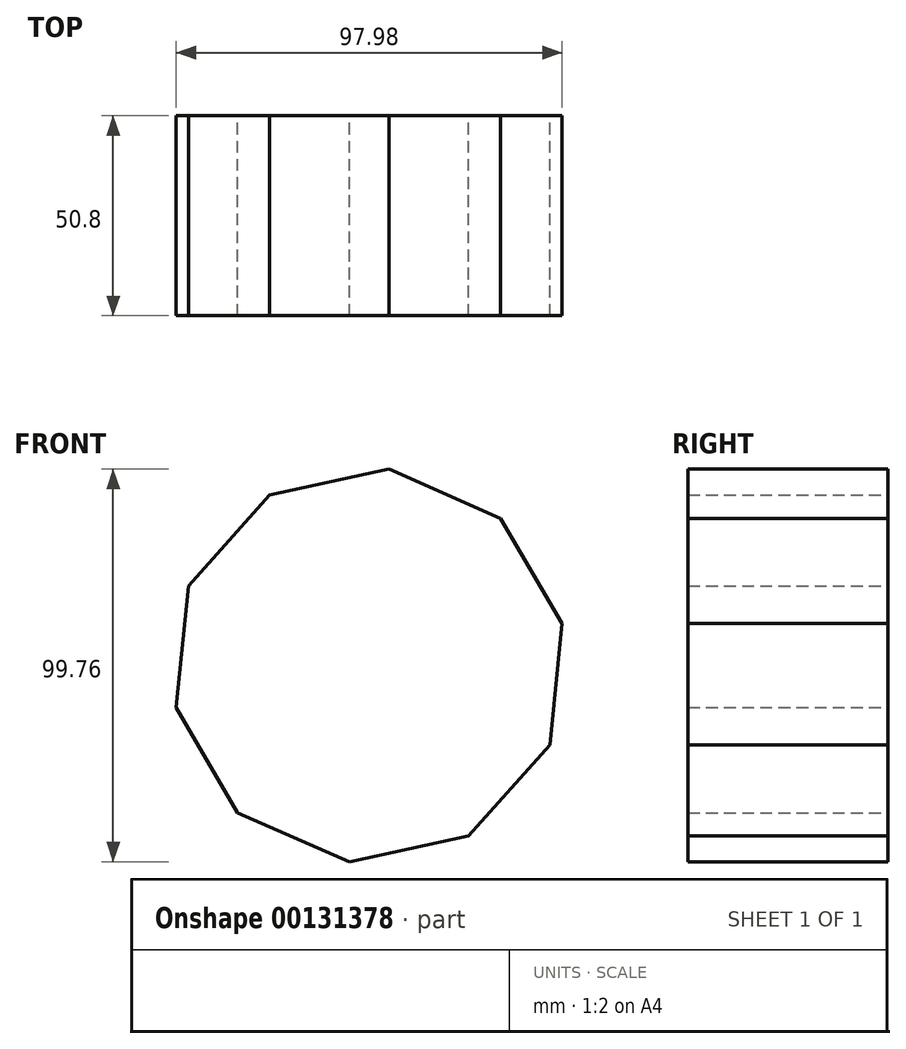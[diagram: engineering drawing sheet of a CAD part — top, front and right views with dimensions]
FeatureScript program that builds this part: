
annotation { "Feature Type Name" : "Feature", "Feature Type Description" : "" }
export const myFeature = defineFeature(function(context is Context, id is Id, definition is map)
    precondition{}
    {
        {
            var Q0;
            Q0=qCreatedBy(makeId("Front.planeOp"),FACE);
            var sketch = newSketch(context, id + "F0", { "sketchPlane" : qUnion([Q0])});
            skCircle(sketch, "E0.cCircle", {"center": v(0, 0) * mm, "radius": 50.13 * mm, "construction": true});
            skLineSegment(sketch, "E0.0", {"start": v(-45.89, 20.18) * mm, "end": v(-25.26, 43.3) * mm});
            skLineSegment(sketch, "E0.1", {"start": v(-25.26, 43.3) * mm, "end": v(5.02, 49.88) * mm});
            skLineSegment(sketch, "E0.2", {"start": v(5.02, 49.88) * mm, "end": v(33.38, 37.4) * mm});
            skLineSegment(sketch, "E0.3", {"start": v(33.38, 37.4) * mm, "end": v(48.99, 10.64) * mm});
            skLineSegment(sketch, "E0.4", {"start": v(48.99, 10.64) * mm, "end": v(45.89, -20.18) * mm});
            skLineSegment(sketch, "E0.5", {"start": v(45.89, -20.18) * mm, "end": v(25.26, -43.3) * mm});
            skLineSegment(sketch, "E0.6", {"start": v(25.26, -43.3) * mm, "end": v(-5.02, -49.88) * mm});
            skLineSegment(sketch, "E0.7", {"start": v(-5.02, -49.88) * mm, "end": v(-33.38, -37.4) * mm});
            skLineSegment(sketch, "E0.8", {"start": v(-33.38, -37.4) * mm, "end": v(-48.99, -10.64) * mm});
            skLineSegment(sketch, "E0.9", {"start": v(-48.99, -10.64) * mm, "end": v(-45.89, 20.18) * mm});
            skSolve(sketch);
        }
        {
            var Q0;
            Q0 = qSketchRegion(id + "F0", true);
            extrude(context, id + "F1", {"entities" : qUnion([Q0]), "depth" : 50.8 * mm});
        }
    });
